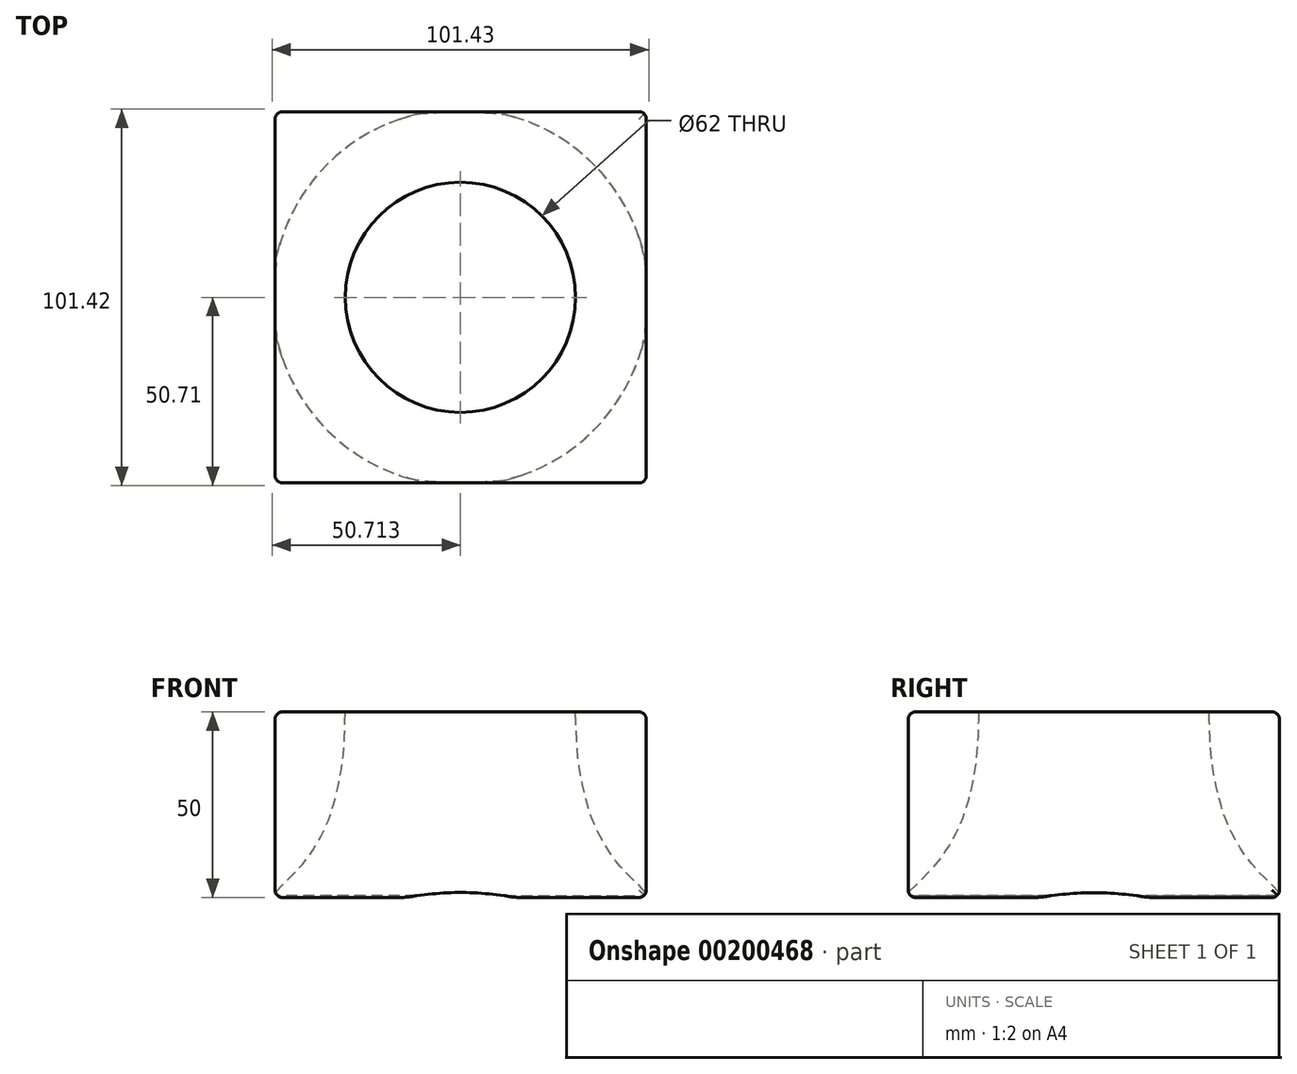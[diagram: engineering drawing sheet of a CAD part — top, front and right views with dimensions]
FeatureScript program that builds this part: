
annotation { "Feature Type Name" : "Feature", "Feature Type Description" : "" }
export const myFeature = defineFeature(function(context is Context, id is Id, definition is map)
    precondition{}
    {
        {
            var Q0;
            Q0=qCreatedBy(makeId("Top.planeOp"),FACE);
            var sketch = newSketch(context, id + "F0", { "sketchPlane" : qUnion([Q0])});
            skLineSegment(sketch, "E0.bottom", {"start": v(-50, 50) * mm, "end": v(50, 50) * mm});
            skLineSegment(sketch, "E0.top", {"start": v(-50, -50) * mm, "end": v(50, -50) * mm});
            skLineSegment(sketch, "E0.left", {"start": v(-50, 50) * mm, "end": v(-50, -50) * mm});
            skLineSegment(sketch, "E0.right", {"start": v(50, 50) * mm, "end": v(50, -50) * mm});
            skPoint(sketch, "E0.middle", {"position": v(0, 0) * mm});
            skSolve(sketch);
        }
        {
            var Q0;
            Q0 = qSketchRegion(id + "F0", true);
            extrude(context, id + "F1", {"entities" : qUnion([Q0]), "depth" : 50 * mm});
        }
        {
            var Q0;
            Q0=qCreatedBy(makeId("Front.planeOp"),FACE);
            var sketch = newSketch(context, id + "F2", { "sketchPlane" : qUnion([Q0])});
            skLineSegment(sketch, "E1", {"start": v(-0.06, -0.4) * mm, "end": v(-0.06, 50.6) * mm});
            skLineSegment(sketch, "E2", {"start": v(-0.06, -0.4) * mm, "end": v(-50.06, -0.4) * mm});
            skLineSegment(sketch, "E3", {"start": v(-0.06, 50.6) * mm, "end": v(-30.06, 50.6) * mm});
            skFitSpline(sketch, "E4.0", {"points": [v(-31.06, 49.84) * mm, v(-31.23, 45.2) * mm, v(-31.7, 37.75) * mm, v(-33.12, 29.42) * mm, v(-34.26, 24.93) * mm, v(-35.3, 21.74) * mm, v(-36.52, 18.79) * mm, v(-38.43, 15.1) * mm, v(-42.48, 9.1) * mm, v(-47.15, 4.18) * mm, v(-50.77, 0.5) * mm]});
            skPoint(sketch, "E5.start.orphan", {"position": v(-50.77, -0.4) * mm});
            skLineSegment(sketch, "E6", {"start": v(-30.06, 50.6) * mm, "end": v(-31.06, 50.6) * mm});
            skLineSegment(sketch, "E7", {"start": v(-31.06, 50.6) * mm, "end": v(-31.06, 49.84) * mm});
            skLineSegment(sketch, "E8", {"start": v(-50.06, -0.4) * mm, "end": v(-50.77, -0.4) * mm});
            skLineSegment(sketch, "E9", {"start": v(-50.77, 0.5) * mm, "end": v(-50.77, -0.4) * mm});
            skSolve(sketch);
        }
        {
            var Q0;
            Q0 = qSketchRegion(id + "F2", true);
            var Q1;
            Q1=sQuery(id+"F2.wireOp",EDGE,"E1");
            revolve(context, id + "F3", {"operationType" : NewBodyOperationType.REMOVE, "entities" : qUnion([Q0]), "axis" : qUnion([Q1]), "revolveType" : RevolveType.FULL, "oppositeDirection" : true});
        }
        {
            var Q0;
            Q0=makeQuery(id+"F1.opExtrude","CAP_EDGE",EDGE,{"disambiguationData":[OSD([sQuery(id+"F0.wireOp",EDGE,"E0.top")])],"isStart":false});
            var Q1;
            Q1=makeQuery(id+"F1.opExtrude","CAP_EDGE",EDGE,{"disambiguationData":[OSD([sQuery(id+"F0.wireOp",EDGE,"E0.left")])],"isStart":false});
            var Q2;
            Q2=makeQuery(id+"F1.opExtrude","CAP_EDGE",EDGE,{"disambiguationData":[OSD([sQuery(id+"F0.wireOp",EDGE,"E0.right")])],"isStart":false});
            var Q3;
            Q3=makeQuery(id+"F1.opExtrude","SWEPT_EDGE",EDGE,{"disambiguationData":[OSD([sQuery(id+"F0.wireOp",EDGE,"E0.top"),sQuery(id+"F0.wireOp",EDGE,"E0.right")])]});
            var Q4;
            Q4=makeQuery(id+"F1.opExtrude","SWEPT_EDGE",EDGE,{"disambiguationData":[OSD([sQuery(id+"F0.wireOp",EDGE,"E0.bottom"),sQuery(id+"F0.wireOp",EDGE,"E0.right")])]});
            var Q5;
            Q5=makeQuery(id+"F1.opExtrude","CAP_EDGE",EDGE,{"disambiguationData":[OSD([sQuery(id+"F0.wireOp",EDGE,"E0.bottom")])],"isStart":false});
            var Q6;
            Q6=makeQuery(id+"F1.opExtrude","SWEPT_EDGE",EDGE,{"disambiguationData":[OSD([sQuery(id+"F0.wireOp",EDGE,"E0.bottom"),sQuery(id+"F0.wireOp",EDGE,"E0.left")])]});
            var Q7;
            {var subQ0=sQuery(id+"F0.wireOp",EDGE,"E0.bottom");var subQ1=sQuery(id+"F0.wireOp",EDGE,"E0.left");Q7=makeQuery(id+"F3.boolean.opBoolean","SPLIT",EDGE,{"disambiguationData":[TD([makeQuery(id+"F1.opExtrude","SWEPT_FACE",FACE,{"disambiguationData":[OSD([subQ1])]})])],"derivedFrom":makeQuery(id+"F1.opExtrude","CAP_EDGE",EDGE,{"disambiguationData":[OSD([subQ0])],"isStart":true})});}
            var Q8;
            {var subQ0=sQuery(id+"F0.wireOp",EDGE,"E0.bottom");var subQ1=sQuery(id+"F0.wireOp",EDGE,"E0.right");Q8=makeQuery(id+"F3.boolean.opBoolean","SPLIT",EDGE,{"disambiguationData":[TD([makeQuery(id+"F1.opExtrude","SWEPT_FACE",FACE,{"disambiguationData":[OSD([subQ0])]})])],"derivedFrom":makeQuery(id+"F1.opExtrude","CAP_EDGE",EDGE,{"disambiguationData":[OSD([subQ1])],"isStart":true})});}
            var Q9;
            {var subQ0=sQuery(id+"F0.wireOp",EDGE,"E0.right");var subQ1=sQuery(id+"F0.wireOp",EDGE,"E0.top");Q9=makeQuery(id+"F3.boolean.opBoolean","SPLIT",EDGE,{"disambiguationData":[TD([makeQuery(id+"F1.opExtrude","SWEPT_FACE",FACE,{"disambiguationData":[OSD([subQ1])]})])],"derivedFrom":makeQuery(id+"F1.opExtrude","CAP_EDGE",EDGE,{"disambiguationData":[OSD([subQ0])],"isStart":true})});}
            var Q10;
            {var subQ0=sQuery(id+"F0.wireOp",EDGE,"E0.bottom");var subQ1=sQuery(id+"F0.wireOp",EDGE,"E0.left");Q10=makeQuery(id+"F3.boolean.opBoolean","SPLIT",EDGE,{"disambiguationData":[TD([makeQuery(id+"F1.opExtrude","SWEPT_FACE",FACE,{"disambiguationData":[OSD([subQ0])]})])],"derivedFrom":makeQuery(id+"F1.opExtrude","CAP_EDGE",EDGE,{"disambiguationData":[OSD([subQ1])],"isStart":true})});}
            var Q11;
            {var subQ0=sQuery(id+"F0.wireOp",EDGE,"E0.right");var subQ1=sQuery(id+"F0.wireOp",EDGE,"E0.top");Q11=makeQuery(id+"F3.boolean.opBoolean","SPLIT",EDGE,{"disambiguationData":[TD([makeQuery(id+"F1.opExtrude","SWEPT_FACE",FACE,{"disambiguationData":[OSD([subQ0])]})])],"derivedFrom":makeQuery(id+"F1.opExtrude","CAP_EDGE",EDGE,{"disambiguationData":[OSD([subQ1])],"isStart":true})});}
            var Q12;
            {var subQ0=sQuery(id+"F0.wireOp",EDGE,"E0.left");var subQ1=sQuery(id+"F0.wireOp",EDGE,"E0.top");Q12=makeQuery(id+"F3.boolean.opBoolean","SPLIT",EDGE,{"disambiguationData":[TD([makeQuery(id+"F1.opExtrude","SWEPT_FACE",FACE,{"disambiguationData":[OSD([subQ0])]})])],"derivedFrom":makeQuery(id+"F1.opExtrude","CAP_EDGE",EDGE,{"disambiguationData":[OSD([subQ1])],"isStart":true})});}
            var Q13;
            {var subQ0=sQuery(id+"F0.wireOp",EDGE,"E0.left");var subQ1=sQuery(id+"F0.wireOp",EDGE,"E0.top");Q13=makeQuery(id+"F3.boolean.opBoolean","SPLIT",EDGE,{"disambiguationData":[TD([makeQuery(id+"F1.opExtrude","SWEPT_FACE",FACE,{"disambiguationData":[OSD([subQ1])]})])],"derivedFrom":makeQuery(id+"F1.opExtrude","CAP_EDGE",EDGE,{"disambiguationData":[OSD([subQ0])],"isStart":true})});}
            var Q14;
            Q14=makeQuery(id+"F1.opExtrude","SWEPT_EDGE",EDGE,{"disambiguationData":[OSD([sQuery(id+"F0.wireOp",EDGE,"E0.top"),sQuery(id+"F0.wireOp",EDGE,"E0.left")])]});
            fillet(context, id + "F4", {"entities" : qUnion([Q0, Q1, Q2, Q3, Q4, Q5, Q6, Q7, Q8, Q9, Q10, Q11, Q12, Q13, Q14]), "radius" : 2 * mm, "tangentPropagation" : true, "allowEdgeOverflow" : false});
        }
    });
